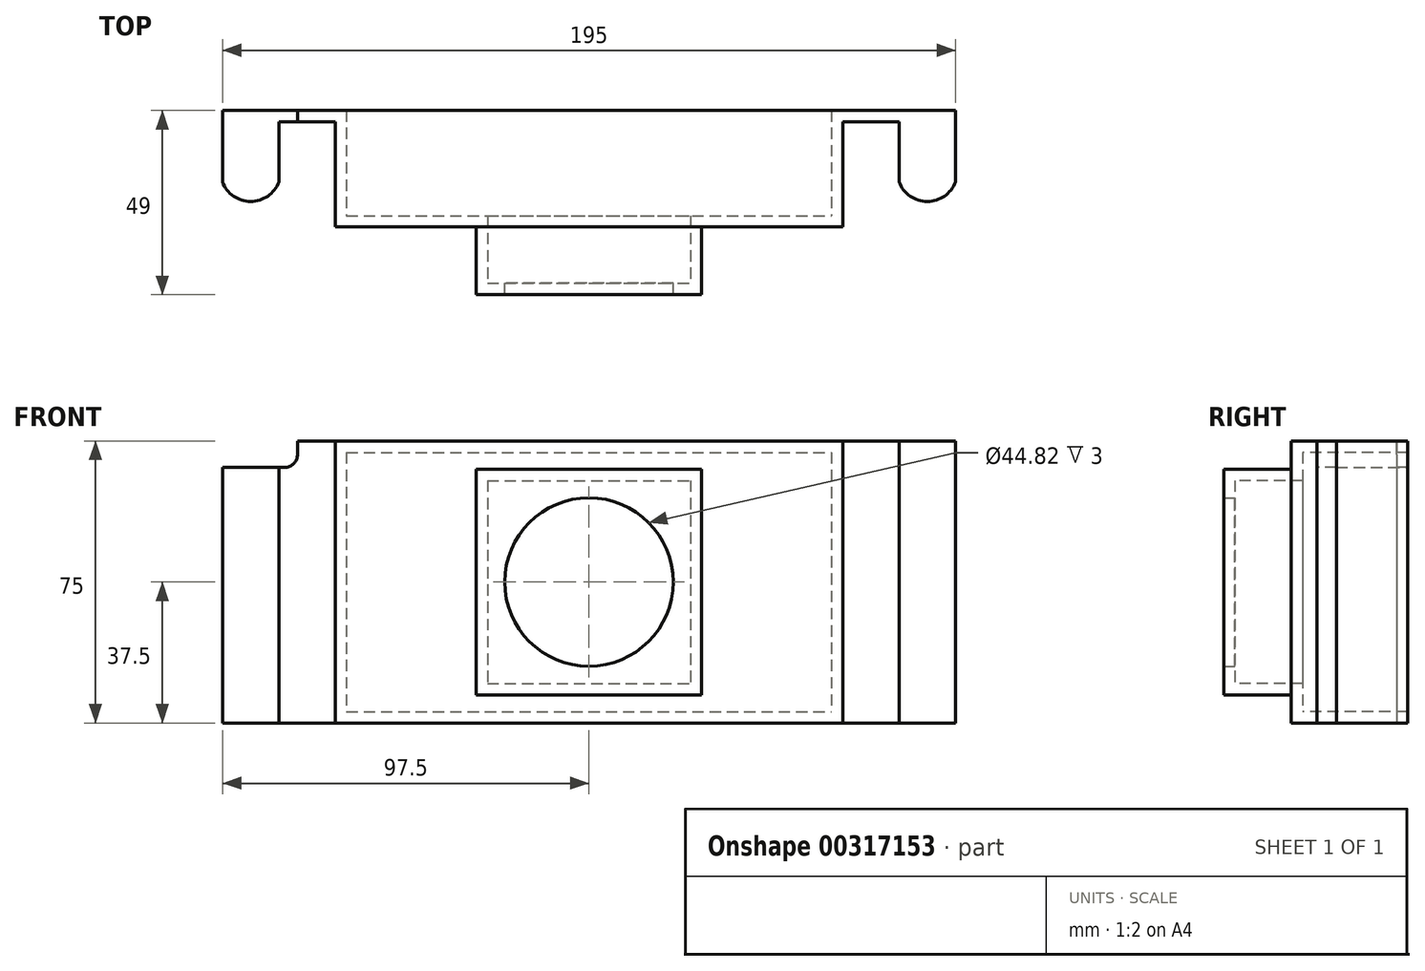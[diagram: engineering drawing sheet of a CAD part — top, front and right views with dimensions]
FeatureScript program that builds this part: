
annotation { "Feature Type Name" : "Feature", "Feature Type Description" : "" }
export const myFeature = defineFeature(function(context is Context, id is Id, definition is map)
    precondition{}
    {
        {
            var Q0;
            Q0=qCreatedBy(makeId("Front.planeOp"),FACE);
            var sketch = newSketch(context, id + "F0", { "sketchPlane" : qUnion([Q0])});
            skLineSegment(sketch, "E0.bottom", {"start": v(30, 30) * mm, "end": v(-30, 30) * mm});
            skLineSegment(sketch, "E0.top", {"start": v(30, -30) * mm, "end": v(-30, -30) * mm});
            skLineSegment(sketch, "E0.left", {"start": v(30, 30) * mm, "end": v(30, -30) * mm});
            skLineSegment(sketch, "E0.right", {"start": v(-30, 30) * mm, "end": v(-30, -30) * mm});
            skPoint(sketch, "E0.middle", {"position": v(0, 0) * mm});
            skCircle(sketch, "E1", {"center": v(0, 0) * mm, "radius": 22.4 * mm});
            skSolve(sketch);
        }
        {
            var Q0;
            Q0 = qSketchRegion(id + "F0", true);
            extrude(context, id + "F1", {"entities" : qUnion([Q0]), "depth" : 3 * mm});
        }
        {
            var Q0;
            Q0=makeQuery(id+"F1.opExtrude","CAP_FACE",FACE,{"disambiguationData":[OSD([sQuery(id+"F0.wireOp",EDGE,"E0.bottom"),sQuery(id+"F0.wireOp",EDGE,"E0.top"),sQuery(id+"F0.wireOp",EDGE,"E0.left"),sQuery(id+"F0.wireOp",EDGE,"E0.right"),sQuery(id+"F0.wireOp",EDGE,"E1")])],"isStart":true});
            var sketch = newSketch(context, id + "F2", { "sketchPlane" : qUnion([Q0])});
            skLineSegment(sketch, "E2.bottom", {"start": v(30, 30) * mm, "end": v(-30, 30) * mm});
            skLineSegment(sketch, "E2.top", {"start": v(30, -30) * mm, "end": v(-30, -30) * mm});
            skLineSegment(sketch, "E2.left", {"start": v(30, 30) * mm, "end": v(30, -30) * mm});
            skLineSegment(sketch, "E2.right", {"start": v(-30, 30) * mm, "end": v(-30, -30) * mm});
            skPoint(sketch, "E2.middle", {"position": v(0, 0) * mm});
            skLineSegment(sketch, "E3.bottom", {"start": v(27, 27) * mm, "end": v(-27, 27) * mm});
            skLineSegment(sketch, "E3.top", {"start": v(27, -27) * mm, "end": v(-27, -27) * mm});
            skLineSegment(sketch, "E3.left", {"start": v(27, 27) * mm, "end": v(27, -27) * mm});
            skLineSegment(sketch, "E3.right", {"start": v(-27, 27) * mm, "end": v(-27, -27) * mm});
            skSolve(sketch);
        }
        {
            var Q0;
            Q0 = qSketchRegion(id + "F2", true);
            extrude(context, id + "F3", {"entities" : qUnion([Q0]), "operationType" : NewBodyOperationType.ADD, "depth" : 15 * mm});
        }
        {
            var Q0;
            Q0=makeQuery(id+"F3.opExtrude","CAP_FACE",FACE,{"disambiguationData":[OSD([sQuery(id+"F2.wireOp",EDGE,"E2.bottom"),sQuery(id+"F2.wireOp",EDGE,"E2.top"),sQuery(id+"F2.wireOp",EDGE,"E2.left"),sQuery(id+"F2.wireOp",EDGE,"E2.right"),sQuery(id+"F2.wireOp",EDGE,"E3.bottom"),sQuery(id+"F2.wireOp",EDGE,"E3.top"),sQuery(id+"F2.wireOp",EDGE,"E3.left"),sQuery(id+"F2.wireOp",EDGE,"E3.right")])],"isStart":false});
            var sketch = newSketch(context, id + "F4", { "sketchPlane" : qUnion([Q0])});
            skLineSegment(sketch, "E4.bottom", {"start": v(67.5, 37.5) * mm, "end": v(-67.5, 37.5) * mm});
            skLineSegment(sketch, "E4.top", {"start": v(67.5, -37.5) * mm, "end": v(-67.5, -37.5) * mm});
            skLineSegment(sketch, "E4.left", {"start": v(67.5, 37.5) * mm, "end": v(67.5, -37.5) * mm});
            skLineSegment(sketch, "E4.right", {"start": v(-67.5, 37.5) * mm, "end": v(-67.5, -37.5) * mm});
            skPoint(sketch, "E4.middle", {"position": v(0, 0) * mm});
            skLineSegment(sketch, "E5.bottom", {"start": v(27, 27) * mm, "end": v(-27, 27) * mm});
            skLineSegment(sketch, "E5.top", {"start": v(27, -27) * mm, "end": v(-27, -27) * mm});
            skLineSegment(sketch, "E5.left", {"start": v(27, 27) * mm, "end": v(27, -27) * mm});
            skLineSegment(sketch, "E5.right", {"start": v(-27, 27) * mm, "end": v(-27, -27) * mm});
            skSolve(sketch);
        }
        {
            var Q0;
            Q0 = qSketchRegion(id + "F4", true);
            extrude(context, id + "F5", {"entities" : qUnion([Q0]), "operationType" : NewBodyOperationType.ADD, "depth" : 3 * mm});
        }
        {
            var Q0;
            Q0=makeQuery(id+"F5.opExtrude","CAP_FACE",FACE,{"disambiguationData":[OSD([sQuery(id+"F4.wireOp",EDGE,"E4.bottom"),sQuery(id+"F4.wireOp",EDGE,"E4.top"),sQuery(id+"F4.wireOp",EDGE,"E4.left"),sQuery(id+"F4.wireOp",EDGE,"E4.right"),sQuery(id+"F4.wireOp",EDGE,"E5.bottom"),sQuery(id+"F4.wireOp",EDGE,"E5.top"),sQuery(id+"F4.wireOp",EDGE,"E5.left"),sQuery(id+"F4.wireOp",EDGE,"E5.right")])],"isStart":false});
            var sketch = newSketch(context, id + "F6", { "sketchPlane" : qUnion([Q0])});
            skLineSegment(sketch, "E6.bottom", {"start": v(67.5, 37.5) * mm, "end": v(-67.5, 37.5) * mm});
            skLineSegment(sketch, "E6.top", {"start": v(67.5, -37.5) * mm, "end": v(-67.5, -37.5) * mm});
            skLineSegment(sketch, "E6.left", {"start": v(67.5, 37.5) * mm, "end": v(67.5, -37.5) * mm});
            skLineSegment(sketch, "E6.right", {"start": v(-67.5, 37.5) * mm, "end": v(-67.5, -37.5) * mm});
            skPoint(sketch, "E6.middle", {"position": v(0, 0) * mm});
            skLineSegment(sketch, "E7.bottom", {"start": v(64.5, 34.5) * mm, "end": v(-64.5, 34.5) * mm});
            skLineSegment(sketch, "E7.top", {"start": v(64.5, -34.5) * mm, "end": v(-64.5, -34.5) * mm});
            skLineSegment(sketch, "E7.left", {"start": v(64.5, 34.5) * mm, "end": v(64.5, -34.5) * mm});
            skLineSegment(sketch, "E7.right", {"start": v(-64.5, 34.5) * mm, "end": v(-64.5, -34.5) * mm});
            skSolve(sketch);
        }
        {
            var Q0;
            Q0 = qSketchRegion(id + "F6", true);
            extrude(context, id + "F7", {"entities" : qUnion([Q0]), "operationType" : NewBodyOperationType.ADD, "depth" : 25 * mm});
        }
        {
            var Q0;
            Q0=makeQuery(id+"F7.opExtrude","CAP_FACE",FACE,{"disambiguationData":[OSD([sQuery(id+"F6.wireOp",EDGE,"E6.bottom"),sQuery(id+"F6.wireOp",EDGE,"E6.top"),sQuery(id+"F6.wireOp",EDGE,"E6.left"),sQuery(id+"F6.wireOp",EDGE,"E6.right"),sQuery(id+"F6.wireOp",EDGE,"E7.bottom"),sQuery(id+"F6.wireOp",EDGE,"E7.top"),sQuery(id+"F6.wireOp",EDGE,"E7.left"),sQuery(id+"F6.wireOp",EDGE,"E7.right")])],"isStart":false});
            var sketch = newSketch(context, id + "F8", { "sketchPlane" : qUnion([Q0])});
            skLineSegment(sketch, "E8.bottom", {"start": v(97.5, 37.5) * mm, "end": v(-97.5, 37.5) * mm});
            skLineSegment(sketch, "E8.top", {"start": v(97.5, -37.5) * mm, "end": v(-97.5, -37.5) * mm});
            skLineSegment(sketch, "E8.left", {"start": v(97.5, 37.5) * mm, "end": v(97.5, -37.5) * mm});
            skLineSegment(sketch, "E8.right", {"start": v(-97.5, 37.5) * mm, "end": v(-97.5, -37.5) * mm});
            skPoint(sketch, "E8.middle", {"position": v(0, 0) * mm});
            skLineSegment(sketch, "E9.bottom", {"start": v(64.5, 34.5) * mm, "end": v(-64.5, 34.5) * mm});
            skLineSegment(sketch, "E9.top", {"start": v(64.5, -34.5) * mm, "end": v(-64.5, -34.5) * mm});
            skLineSegment(sketch, "E9.left", {"start": v(64.5, 34.5) * mm, "end": v(64.5, -34.5) * mm});
            skLineSegment(sketch, "E9.right", {"start": v(-64.5, 34.5) * mm, "end": v(-64.5, -34.5) * mm});
            skSolve(sketch);
        }
        {
            var Q0;
            Q0 = qSketchRegion(id + "F8", true);
            extrude(context, id + "F9", {"entities" : qUnion([Q0]), "operationType" : NewBodyOperationType.ADD, "depth" : 3 * mm});
        }
        {
            var Q0;
            {var subQ0=sQuery(id+"F8.wireOp",EDGE,"E8.left");var subQ1=sQuery(id+"F8.wireOp",EDGE,"E8.bottom");var subQ2=sQuery(id+"F8.wireOp",EDGE,"E8.top");Q0=makeQuery(id+"F9.boolean.opBoolean","SPLIT",FACE,{"disambiguationData":[TD([makeQuery(id+"F5.opExtrude","SWEPT_FACE",FACE,{"disambiguationData":[OSD([sQuery(id+"F4.wireOp",EDGE,"E4.left")])]})])],"derivedFrom":makeQuery(id+"F9.opExtrude","CAP_FACE",FACE,{"disambiguationData":[OSD([subQ1,subQ2,subQ0,sQuery(id+"F8.wireOp",EDGE,"E8.right"),sQuery(id+"F8.wireOp",EDGE,"E9.bottom"),sQuery(id+"F8.wireOp",EDGE,"E9.top"),sQuery(id+"F8.wireOp",EDGE,"E9.left"),sQuery(id+"F8.wireOp",EDGE,"E9.right")])],"isStart":true})});}
            var sketch = newSketch(context, id + "F10", { "sketchPlane" : qUnion([Q0])});
            skLineSegment(sketch, "E10.top", {"start": v(-97.5, -37.5) * mm, "end": v(-82.5, -37.5) * mm});
            skLineSegment(sketch, "E11", {"start": v(-97.5, 30.5) * mm, "end": v(-82.5, 30.5) * mm});
            skLineSegment(sketch, "E12", {"start": v(-82.5, 30.5) * mm, "end": v(-82.5, -37.5) * mm});
            skLineSegment(sketch, "E13", {"start": v(-97.5, -37.5) * mm, "end": v(-97.5, 30.5) * mm});
            skSolve(sketch);
        }
        {
            var Q0;
            Q0 = qSketchRegion(id + "F10", true);
            extrude(context, id + "F11", {"entities" : qUnion([Q0]), "operationType" : NewBodyOperationType.ADD, "depth" : 25 * mm});
        }
        {
            var Q0;
            {var subQ0=sQuery(id+"F8.wireOp",EDGE,"E8.bottom");var subQ1=sQuery(id+"F8.wireOp",EDGE,"E8.top");var subQ2=sQuery(id+"F8.wireOp",EDGE,"E8.right");Q0=makeQuery(id+"F9.boolean.opBoolean","SPLIT",FACE,{"disambiguationData":[TD([makeQuery(id+"F5.opExtrude","SWEPT_FACE",FACE,{"disambiguationData":[OSD([sQuery(id+"F4.wireOp",EDGE,"E4.right")])]})])],"derivedFrom":makeQuery(id+"F9.opExtrude","CAP_FACE",FACE,{"disambiguationData":[OSD([subQ0,subQ1,sQuery(id+"F8.wireOp",EDGE,"E8.left"),subQ2,sQuery(id+"F8.wireOp",EDGE,"E9.bottom"),sQuery(id+"F8.wireOp",EDGE,"E9.top"),sQuery(id+"F8.wireOp",EDGE,"E9.left"),sQuery(id+"F8.wireOp",EDGE,"E9.right")])],"isStart":true})});}
            var sketch = newSketch(context, id + "F12", { "sketchPlane" : qUnion([Q0])});
            skLineSegment(sketch, "E14.bottom", {"start": v(97.5, 37.5) * mm, "end": v(82.5, 37.5) * mm});
            skLineSegment(sketch, "E14.top", {"start": v(97.5, -37.5) * mm, "end": v(82.5, -37.5) * mm});
            skLineSegment(sketch, "E14.left", {"start": v(97.5, 37.5) * mm, "end": v(97.5, -37.5) * mm});
            skLineSegment(sketch, "E14.right", {"start": v(82.5, 37.5) * mm, "end": v(82.5, -37.5) * mm});
            skSolve(sketch);
        }
        {
            var Q0;
            Q0 = qSketchRegion(id + "F12", true);
            extrude(context, id + "F13", {"entities" : qUnion([Q0]), "operationType" : NewBodyOperationType.ADD, "depth" : 25 * mm});
        }
        {
            var Q0;
            Q0=makeQuery(id+"F13.boolean.opBoolean","MERGE",FACE,{"derivedFrom":[makeQuery(id+"F11.boolean.opBoolean","MERGE",FACE,{"derivedFrom":[makeQuery(id+"F9.boolean.opBoolean","MERGE",FACE,{"derivedFrom":[makeQuery(id+"F7.boolean.opBoolean","MERGE",FACE,{"derivedFrom":[makeQuery(id+"F5.opExtrude","SWEPT_FACE",FACE,{"disambiguationData":[OSD([sQuery(id+"F4.wireOp",EDGE,"E4.bottom")])]}),makeQuery(id+"F7.opExtrude","SWEPT_FACE",FACE,{"disambiguationData":[OSD([sQuery(id+"F6.wireOp",EDGE,"E6.bottom")])]})]}),makeQuery(id+"F9.opExtrude","SWEPT_FACE",FACE,{"disambiguationData":[OSD([sQuery(id+"F8.wireOp",EDGE,"E8.bottom")])]})]}),makeQuery(id+"F11.opExtrude","SWEPT_FACE",FACE,{"disambiguationData":[OSD([sQuery(id+"F10.wireOp",EDGE,"E10.bottom")])]})]}),makeQuery(id+"F13.opExtrude","SWEPT_FACE",FACE,{"disambiguationData":[OSD([sQuery(id+"F12.wireOp",EDGE,"E14.bottom")])]})]});
            var sketch = newSketch(context, id + "F14", { "sketchPlane" : qUnion([Q0])});
            skArc(sketch, "E15", {"start": v(-97.5, 27) * mm, "mid": v(-90, 21.78) * mm, "end": v(-82.5, 27) * mm});
            skArc(sketch, "E16", {"start": v(82.5, 27) * mm, "mid": v(90, 21.78) * mm, "end": v(97.5, 27) * mm});
            skLineSegment(sketch, "E17", {"start": v(-97.5, 27) * mm, "end": v(-97.5, 18) * mm});
            skLineSegment(sketch, "E18", {"start": v(-97.5, 18) * mm, "end": v(-82.5, 18) * mm});
            skLineSegment(sketch, "E19", {"start": v(-82.5, 18) * mm, "end": v(-82.5, 27) * mm});
            skLineSegment(sketch, "E20", {"start": v(82.5, 27) * mm, "end": v(82.5, 18) * mm});
            skLineSegment(sketch, "E21", {"start": v(82.5, 18) * mm, "end": v(97.5, 18) * mm});
            skLineSegment(sketch, "E22", {"start": v(97.5, 18) * mm, "end": v(97.5, 27) * mm});
            skSolve(sketch);
        }
        {
            var Q0;
            Q0 = qSketchRegion(id + "F14", true);
            extrude(context, id + "F15", {"entities" : qUnion([Q0]), "operationType" : NewBodyOperationType.REMOVE, "oppositeDirection" : true, "depth" : 200 * mm});
        }
        {
            var Q0;
            {var subQ0=sQuery(id+"F8.wireOp",EDGE,"E8.left");var subQ1=sQuery(id+"F8.wireOp",EDGE,"E8.bottom");var subQ2=sQuery(id+"F8.wireOp",EDGE,"E8.top");Q0=makeQuery(id+"F9.boolean.opBoolean","SPLIT",FACE,{"disambiguationData":[TD([makeQuery(id+"F5.opExtrude","SWEPT_FACE",FACE,{"disambiguationData":[OSD([sQuery(id+"F4.wireOp",EDGE,"E4.left")])]})])],"derivedFrom":makeQuery(id+"F9.opExtrude","CAP_FACE",FACE,{"disambiguationData":[OSD([subQ1,subQ2,subQ0,sQuery(id+"F8.wireOp",EDGE,"E8.right"),sQuery(id+"F8.wireOp",EDGE,"E9.bottom"),sQuery(id+"F8.wireOp",EDGE,"E9.top"),sQuery(id+"F8.wireOp",EDGE,"E9.left"),sQuery(id+"F8.wireOp",EDGE,"E9.right")])],"isStart":true})});}
            var sketch = newSketch(context, id + "F16", { "sketchPlane" : qUnion([Q0])});
            skLineSegment(sketch, "E23", {"start": v(-82.5, 37.5) * mm, "end": v(-97.5, 37.5) * mm});
            skLineSegment(sketch, "E24", {"start": v(-97.5, 37.5) * mm, "end": v(-97.5, 30.5) * mm});
            skLineSegment(sketch, "E25", {"start": v(-97.5, 30.5) * mm, "end": v(-97.5, 37.5) * mm});
            skLineSegment(sketch, "E26", {"start": v(-82.5, 30.5) * mm, "end": v(-97.5, 30.5) * mm});
            skLineSegment(sketch, "E27", {"start": v(-82.5, 30.5) * mm, "end": v(-77.5, 30.5) * mm});
            skLineSegment(sketch, "E28", {"start": v(-77.5, 30.5) * mm, "end": v(-77.5, 37.5) * mm});
            skLineSegment(sketch, "E29", {"start": v(-77.5, 37.5) * mm, "end": v(-82.5, 37.5) * mm});
            skSolve(sketch);
        }
        {
            var Q0;
            Q0 = qSketchRegion(id + "F16", true);
            extrude(context, id + "F17", {"entities" : qUnion([Q0]), "operationType" : NewBodyOperationType.REMOVE, "oppositeDirection" : true, "depth" : 25 * mm});
        }
        {
            var Q0;
            Q0=makeQuery(id+"F17.boolean.opBoolean","COPY",EDGE,{"derivedFrom":makeQuery(id+"F17.opExtrude","SWEPT_EDGE",EDGE,{"disambiguationData":[OSD([sQuery(id+"F16.wireOp",EDGE,"E27"),sQuery(id+"F16.wireOp",EDGE,"E28")])]})});
            var Q1;
            Q1=makeQuery(id+"F17.boolean.opBoolean","COPY",EDGE,{"derivedFrom":makeQuery(id+"F17.opExtrude","SWEPT_EDGE",EDGE,{"disambiguationData":[OSD([sQuery(id+"F8.wireOp",EDGE,"E8.bottom"),sQuery(id+"F16.wireOp",EDGE,"E28"),sQuery(id+"F16.wireOp",EDGE,"E29")])]})});
            fillet(context, id + "F18", {"entities" : qUnion([Q0, Q1]), "radius" : 3.5 * mm, "tangentPropagation" : true, "allowEdgeOverflow" : false});
        }
        {
            var Q0;
            Q0=makeQuery(id+"F19.boolean.opBoolean","MERGE",FACE,{"derivedFrom":[makeQuery(id+"F3.boolean.opBoolean","MERGE",FACE,{"derivedFrom":[makeQuery(id+"F1.opExtrude","SWEPT_FACE",FACE,{"disambiguationData":[OSD([sQuery(id+"F0.wireOp",EDGE,"E0.bottom")])]}),makeQuery(id+"F3.opExtrude","SWEPT_FACE",FACE,{"disambiguationData":[OSD([sQuery(id+"F2.wireOp",EDGE,"E2.bottom")])]})]}),makeQuery(id+"F19.opExtrude","SWEPT_FACE",FACE,{"disambiguationData":[OSD([sQuery(id+"Fg7M6V97ZkYJ0yG_1.wireOp",EDGE,"ihL5YEDn-t8Oy-xYXL-v36N-uPn2xZnvlxlS.bottom")])]})]});
            var sketch = newSketch(context, id + "F20", { "sketchPlane" : qUnion([Q0])});
            skLineSegment(sketch, "E30", {"start": v(-50, 15) * mm, "end": v(-30, -3) * mm});
            skLineSegment(sketch, "E31", {"start": v(-30, -3) * mm, "end": v(-50, -3) * mm});
            skLineSegment(sketch, "E32", {"start": v(-50, -3) * mm, "end": v(-50, 15) * mm});
            skSolve(sketch);
        }
        {
            var Q0;
            Q0 = qSketchRegion(id + "F20", true);
            extrude(context, id + "F21", {"entities" : qUnion([Q0]), "operationType" : NewBodyOperationType.REMOVE, "oppositeDirection" : true, "depth" : 60 * mm});
        }
    });
